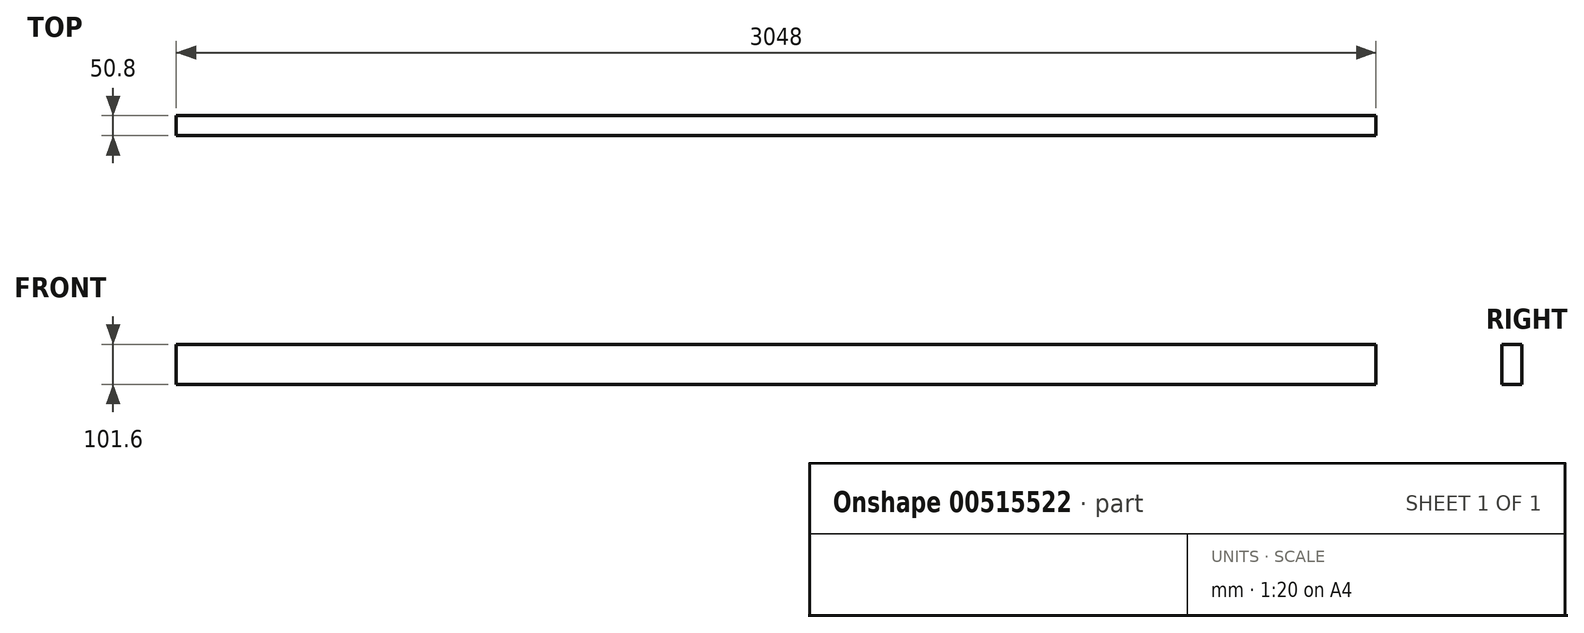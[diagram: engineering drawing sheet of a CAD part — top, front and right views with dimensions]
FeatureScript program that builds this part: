
annotation { "Feature Type Name" : "Feature", "Feature Type Description" : "" }
export const myFeature = defineFeature(function(context is Context, id is Id, definition is map)
    precondition{}
    {
        {
            var Q0;
            Q0=qCreatedBy(makeId("Right.planeOp"),FACE);
            var sketch = newSketch(context, id + "F0", { "sketchPlane" : qUnion([Q0])});
            skLineSegment(sketch, "E0.bottom", {"start": v(25.4, 50.8) * mm, "end": v(-25.4, 50.8) * mm});
            skLineSegment(sketch, "E0.top", {"start": v(25.4, -50.8) * mm, "end": v(-25.4, -50.8) * mm});
            skLineSegment(sketch, "E0.left", {"start": v(25.4, 50.8) * mm, "end": v(25.4, -50.8) * mm});
            skLineSegment(sketch, "E0.right", {"start": v(-25.4, 50.8) * mm, "end": v(-25.4, -50.8) * mm});
            skPoint(sketch, "E0.middle", {"position": v(0, 0) * mm});
            skSolve(sketch);
        }
        {
            var Q0;
            Q0=makeQuery(id+"F0.imprint","IMPRINT",FACE,{"disambiguationData":[TD([[makeQuery(id+"F0.imprint","IMPRINT",EDGE,{"derivedFrom":sQuery(id+"F0.wireOp",EDGE,"E0.bottom")}),1.0]])]});
            extrude(context, id + "F1", {"entities" : qUnion([Q0]), "oppositeDirection" : true, "depth" : 3048 * mm, "offsetDistance" : 25.4 * mm});
        }
    });
